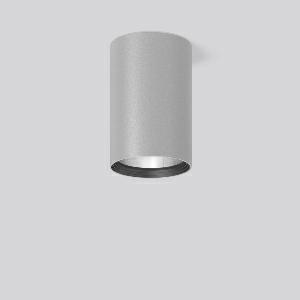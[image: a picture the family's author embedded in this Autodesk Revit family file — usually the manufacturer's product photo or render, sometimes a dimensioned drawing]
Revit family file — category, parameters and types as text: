
# Revit family: heledon_maxi_a_931226_004_0977
name_source: partatom
category: Lighting Fixtures
units: mm (PartAtom-declared; Revit-internal decimal feet)

## family parameters
Cut with Voids When Loaded = No
Host = Face
Light Source = No
Part Type = Normal
Room Calculation Point = No
Round Connector Dimension = Use Diameter
Shared = No

## types (1)
- HELEDON maxi A (1 x LED Modul 930, 4150 lm, 3000)
    Apparent Load = 35 VA
    Approval mark = CE
    CIE Flux Codes = 97 100 100 100 100
    Color Rendering = 90
    Color Temperature = 3000
    Default Elevation = 1800 mm
    Description = Series: HELEDON maxi
Cylindrical surface-mounted downlight. Housing: die-cast aluminium, powder-coated. Internal ceiling frame polycarbonate with bayonet mounting. Black plastic ring and recessed LED to prevent glare from the side. Optical assembly with reflector made of MIRO-Silver with 98% total light reflection for outstanding efficiency - can be changed without tools. Best colour rendering index Ra>90. Suitable for Ceiling mounting. Easy installation with a separate ceiling frame with bayonet mounting and plug connection. Driver integrated. Connected via plug-in connector. High quality converter without flickering and stroboscopic effect. The following accessories can be mounted without use of tools: interchangeable lenses, decorative glasses, honeycomb louvre, clear and frosted diffusers, white interchangeable plastic ring. 
Colour: silver
Diameter: 123 mm
Height: 183 mm
Lamp: LED
Socket: without socket
Colour temperature: 3000K
Colour rendering index (CRI): 92
System power: 35 W
Rated luminous flux: 4150 lm
Luminous efficiency: 119 lm/W
Control gear: Regulated power supply
Protection class: I
Type of protection: IP 20
    Height = 183 mm
    Lamp = 1 x LED Modul 930
    Lamp Light Flux = 4150 lm
    Lamp count = 1
    Length = 123 mm
    Lifetime = 50000 h
    Luminous efficacy = 119 lm/W
    Manufacturer = RZB
    ModVariant = No
    Model = 931226.004
    Mounting Place = Ceiling
    Mounting Type = Surface mounted
    Number of Poles = 1
    OnlyDefault = Yes
    Power Factor = 1
    Product Name = HELEDON maxi A
    Product group = Surface mounted downlights
    ProductGroupID = 302
    Protection Class = Protection class I
    Protection Degree = IP 20
    RLX_Detail_Level = 1
    RLX_Emergency_Light_Flux = 0 lm
    RLX_Emergency_Type = 0
    RLX_Emergency_Type_DB = No
    RlxData = <blob elided: 101025 chars, md5=754e10f4>
    Socket = socket
    Standby Power = 0 W
    System Light Flux = 4150 lm
    System Power = 35 W
    Type Comments = Product without accessories
    Type Image = 931192.004.jpg
    URL = http://relux.com
    VarID = ---
    Voltage = 230 V
    Voltage Range = 220-240 V
    Weight = 0.00 kg
    Width = 0 mm  [stored 0 ft]

note: [stored X ft] marks values corroborated as IEEE doubles in the binary element streams (Revit-internal decimal feet)

## geometry (parser evidence)
native form markers: Blend x4, Sweep x12
no freeform markers — native parametric forms only
